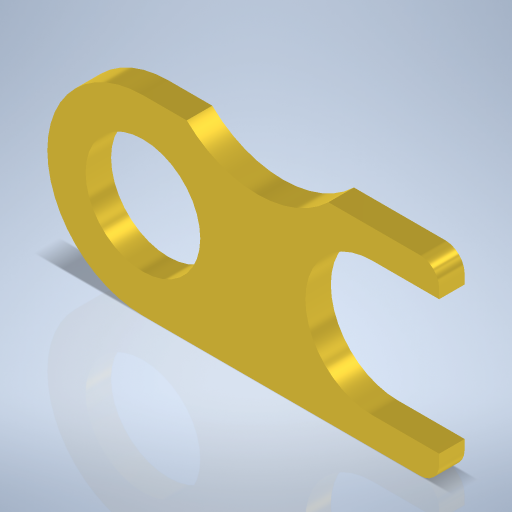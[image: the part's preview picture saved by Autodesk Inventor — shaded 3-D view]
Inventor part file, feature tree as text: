
AUTODESK INVENTOR PART (.ipt)
format: ipt  version: 2024 (Build 280153000, 153)  size: 256,512 bytes
history: native  units: mm
features: extrude x1, sketch x1
ambient origin geometry x8: Origin, YZ Plane, XZ Plane, XY Plane, X Axis, Y Axis, Z Axis, Center Point
bodies: Volumenkörper1 (feature_tree)
feature tree (2):
  extrude  "Extrusion1"  Depth=10.5mm
  sketch  "Skizze1"  dims[d0=15.0mm d1=10.5mm d2=18.0mm d3=1.5mm d4=10.5mm d5=9.0mm d6=2.0mm d7=0.0mm d8=8.0mm d9=9.0mm]
